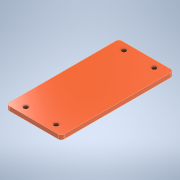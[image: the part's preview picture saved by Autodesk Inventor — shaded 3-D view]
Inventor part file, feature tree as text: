
AUTODESK INVENTOR PART (.ipt)
format: ipt  version: 2021 (Build 250183000, 183)  size: 163,328 bytes
history: native  units: mm
features: sketch x2, extrude x2, fillet x2, hole x1, projected_geometry x1
ambient origin geometry x8: Origin, YZ Plane, XZ Plane, XY Plane, X Axis, Y Axis, Z Axis, Center Point
bodies: Solid1 (feature_tree)
feature tree (8):
  sketch  "Sketch1"  dims[d0=43.0mm d1=62.0mm d2=0.5mm d3=3.0mm d4=12.0mm d5=21.0mm d6=21.0mm d7=12.0mm d8=22.0mm d9=22.0mm d10=5.0mm]
  extrude  "Extrusion1"  Depth=3.0mm
  hole  "Hole1"  [1 undecoded]
  fillet  "Fillet1"  Radius=22.0mm
  extrude  "Extrusion2"  Depth=2.0mm
  fillet  "Fillet2"  Radius=2.0mm
  sketch  "Sketch2"  dims[d11=5.0mm d12=3.0mm d13=0.0mm d14=3.2mm d15=6.0mm d16=4.0mm d17=2.0mm d18=90.0deg d19=8.0mm d20=20.594885mm d28=22.0mm d29=22.0mm d30=2.0mm d31=38.0mm d32=10.5mm d34=21.0mm d35=0.0mm d36=0.0mm d37=2.0mm]
  projected_geometry  "Projected Loop1"
note: 1 required parameter value undecoded (feature->parameter linkage not recoverable at this tier; creation-order binding heuristic only, values carry confidence <= 0.55)
